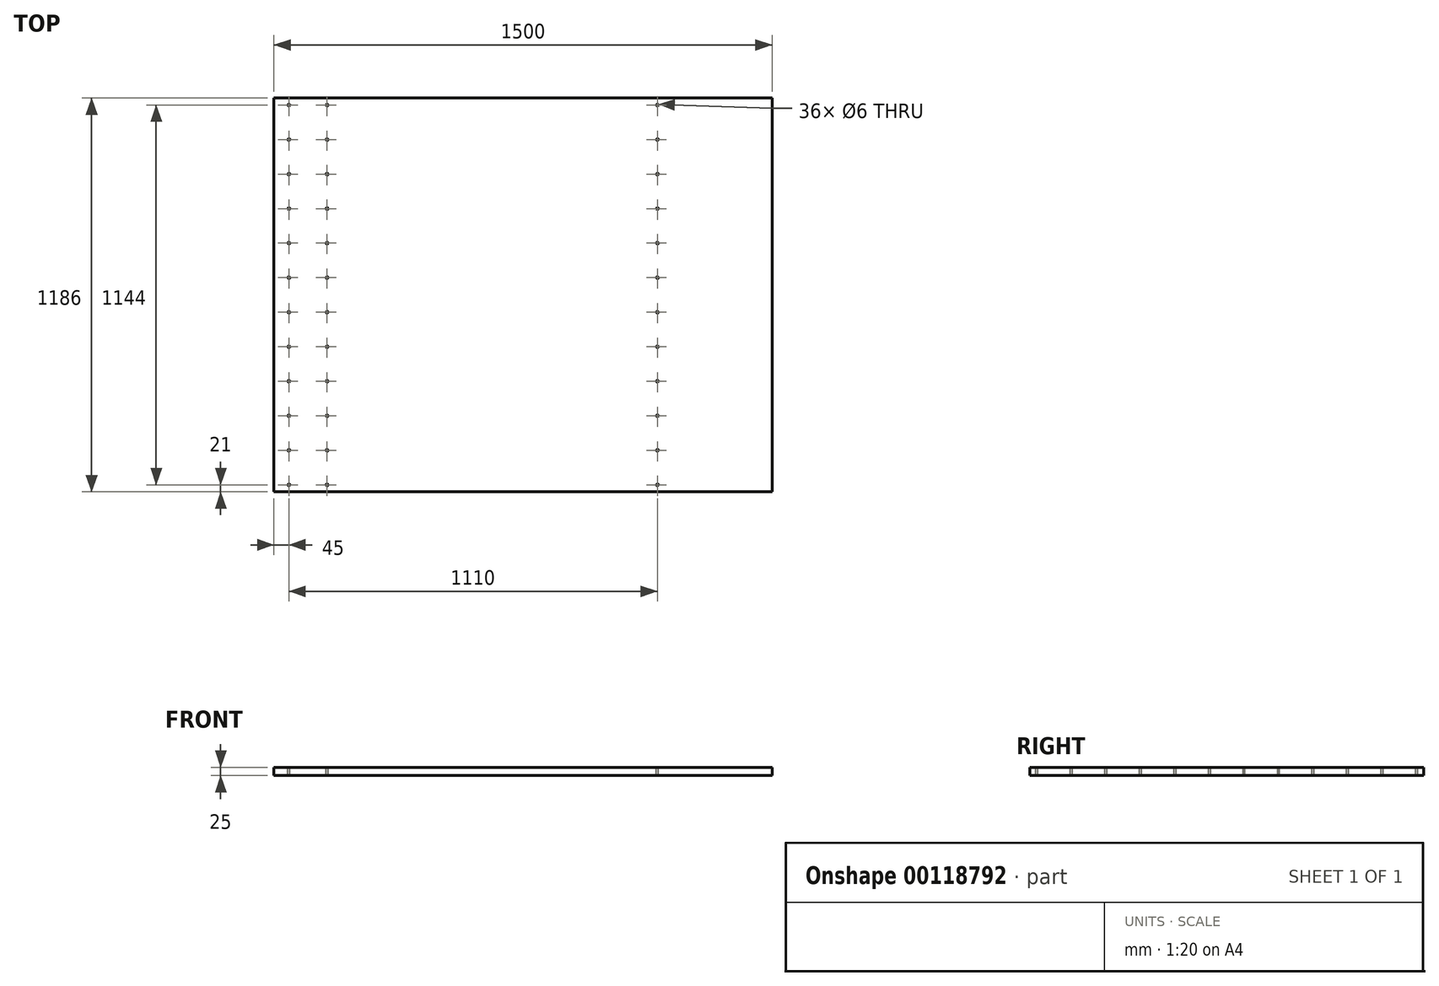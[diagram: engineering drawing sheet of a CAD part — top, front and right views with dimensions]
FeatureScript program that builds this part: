
annotation { "Feature Type Name" : "Feature", "Feature Type Description" : "" }
export const myFeature = defineFeature(function(context is Context, id is Id, definition is map)
    precondition{}
    {
        {
            var Q0;
            Q0=qCreatedBy(makeId("Top.planeOp"),FACE);
            var sketch = newSketch(context, id + "F0", { "sketchPlane" : qUnion([Q0])});
            skLineSegment(sketch, "E0.bottom", {"start": v(0, 0) * mm, "end": v(1500, 0) * mm});
            skLineSegment(sketch, "E0.top", {"start": v(0, 1186) * mm, "end": v(1500, 1186) * mm});
            skLineSegment(sketch, "E0.left", {"start": v(0, 0) * mm, "end": v(0, 1186) * mm});
            skLineSegment(sketch, "E0.right", {"start": v(1500, 0) * mm, "end": v(1500, 1186) * mm});
            skSolve(sketch);
        }
        {
            var Q0;
            Q0 = qSketchRegion(id + "F0", true);
            extrude(context, id + "F1", {"entities" : qUnion([Q0]), "oppositeDirection" : true, "depth" : 25 * mm, "offsetDistance" : 25 * mm});
        }
        {
            var Q0;
            Q0=makeQuery(id+"F1.opExtrude","CAP_FACE",FACE,{"disambiguationData":[OSD([sQuery(id+"F0.wireOp",EDGE,"E0.bottom"),sQuery(id+"F0.wireOp",EDGE,"E0.top"),sQuery(id+"F0.wireOp",EDGE,"E0.left"),sQuery(id+"F0.wireOp",EDGE,"E0.right")])],"isStart":true});
            var sketch = newSketch(context, id + "F2", { "sketchPlane" : qUnion([Q0])});
            skPoint(sketch, "E1", {"position": v(45, 21) * mm});
            skCircle(sketch, "E2", {"center": v(45, 21) * mm, "radius": 3 * mm});
            skCircle(sketch, "E3.0.1.0", {"center": v(45, 125) * mm, "radius": 3 * mm});
            skCircle(sketch, "E3.0.2.0", {"center": v(45, 229) * mm, "radius": 3 * mm});
            skCircle(sketch, "E3.0.3.0", {"center": v(45, 333) * mm, "radius": 3 * mm});
            skCircle(sketch, "E3.0.4.0", {"center": v(45, 437) * mm, "radius": 3 * mm});
            skCircle(sketch, "E3.0.5.0", {"center": v(45, 541) * mm, "radius": 3 * mm});
            skCircle(sketch, "E3.0.6.0", {"center": v(45, 645) * mm, "radius": 3 * mm});
            skCircle(sketch, "E3.0.7.0", {"center": v(45, 749) * mm, "radius": 3 * mm});
            skCircle(sketch, "E3.0.8.0", {"center": v(45, 853) * mm, "radius": 3 * mm});
            skCircle(sketch, "E3.0.9.0", {"center": v(45, 957) * mm, "radius": 3 * mm});
            skCircle(sketch, "E3.0.10.0", {"center": v(45, 1061) * mm, "radius": 3 * mm});
            skCircle(sketch, "E3.0.11.0", {"center": v(45, 1165) * mm, "radius": 3 * mm});
            skLineSegment(sketch, "E3.direction1", {"start": v(45, 21) * mm, "end": v(160, 21) * mm, "construction": true});
            skLineSegment(sketch, "E3.direction2", {"start": v(45, 21) * mm, "end": v(45, 125) * mm, "construction": true});
            skCircle(sketch, "E4.0.1.0", {"center": v(160, 21) * mm, "radius": 3 * mm});
            skCircle(sketch, "E4.0.1.1", {"center": v(160, 125) * mm, "radius": 3 * mm});
            skCircle(sketch, "E4.0.1.2", {"center": v(160, 229) * mm, "radius": 3 * mm});
            skCircle(sketch, "E4.0.1.3", {"center": v(160, 333) * mm, "radius": 3 * mm});
            skCircle(sketch, "E4.0.1.4", {"center": v(160, 437) * mm, "radius": 3 * mm});
            skCircle(sketch, "E4.0.1.5", {"center": v(160, 541) * mm, "radius": 3 * mm});
            skCircle(sketch, "E4.0.1.6", {"center": v(160, 645) * mm, "radius": 3 * mm});
            skCircle(sketch, "E4.0.1.7", {"center": v(160, 749) * mm, "radius": 3 * mm});
            skCircle(sketch, "E4.0.1.8", {"center": v(160, 853) * mm, "radius": 3 * mm});
            skCircle(sketch, "E4.0.1.9", {"center": v(160, 957) * mm, "radius": 3 * mm});
            skCircle(sketch, "E4.0.1.10", {"center": v(160, 1061) * mm, "radius": 3 * mm});
            skCircle(sketch, "E4.0.1.11", {"center": v(160, 1165) * mm, "radius": 3 * mm});
            skCircle(sketch, "E5.1.0.0", {"center": v(1155, 1165) * mm, "radius": 3 * mm});
            skCircle(sketch, "E5.1.0.1", {"center": v(1155, 1061) * mm, "radius": 3 * mm});
            skCircle(sketch, "E5.1.0.2", {"center": v(1155, 957) * mm, "radius": 3 * mm});
            skCircle(sketch, "E5.1.0.3", {"center": v(1155, 749) * mm, "radius": 3 * mm});
            skCircle(sketch, "E5.1.0.4", {"center": v(1155, 541) * mm, "radius": 3 * mm});
            skCircle(sketch, "E5.1.0.5", {"center": v(1155, 333) * mm, "radius": 3 * mm});
            skCircle(sketch, "E5.1.0.6", {"center": v(1155, 125) * mm, "radius": 3 * mm});
            skCircle(sketch, "E5.1.0.7", {"center": v(1155, 853) * mm, "radius": 3 * mm});
            skCircle(sketch, "E5.1.0.8", {"center": v(1155, 645) * mm, "radius": 3 * mm});
            skCircle(sketch, "E5.1.0.9", {"center": v(1155, 437) * mm, "radius": 3 * mm});
            skCircle(sketch, "E5.1.0.10", {"center": v(1155, 229) * mm, "radius": 3 * mm});
            skCircle(sketch, "E5.1.0.11", {"center": v(1155, 21) * mm, "radius": 3 * mm});
            skLineSegment(sketch, "E5.direction1", {"start": v(160, 21) * mm, "end": v(1155, 21) * mm, "construction": true});
            skSolve(sketch);
        }
        {
            var Q0;
            Q0 = qSketchRegion(id + "F2", true);
            extrude(context, id + "F3", {"entities" : qUnion([Q0]), "operationType" : NewBodyOperationType.REMOVE, "oppositeDirection" : true, "depth" : 25 * mm, "offsetDistance" : 25 * mm});
        }
    });
